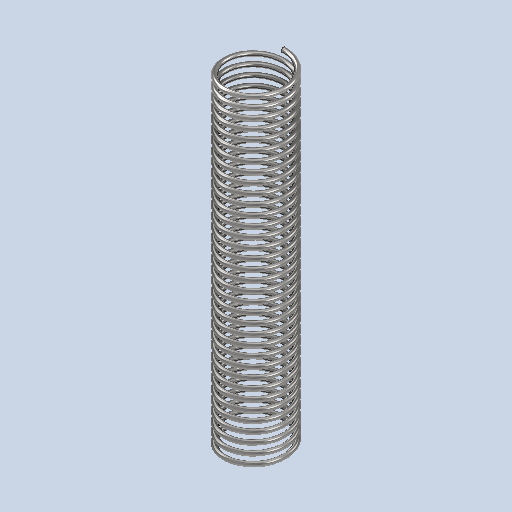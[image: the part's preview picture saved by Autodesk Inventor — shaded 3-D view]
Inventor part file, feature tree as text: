
AUTODESK INVENTOR PART (.ipt)
format: ipt  version: 2025 (Build 290162010, 162A)  size: 1,893,376 bytes
history: native  units: mm
features: sketch x97, plane x32, other x32, sweep x22, extrude x10, helix x4
ambient origin geometry x8: Origin, YZ Plane, XZ Plane, XY Plane, X Axis, Y Axis, Z Axis, Center Point
bodies: Solid1 (feature_tree)
feature tree (197):
  sketch  "3D Sketch2"
  plane  "ArbeitsebeneSweeping1"
  sweep  "Sweep1"
  other  "Erste Umdrehung mit Ösentyp 0(Rechts)"
  sketch  "Sketch8"  dims[d5=0.0mm d6=90.0deg d7=90.0deg d8=0.0mm d9=0.0mm d12=0.2mm]
  plane  "ArbeitsebeneExtrusion7"
  sketch  "Sketch10"  dims[d17=90.0deg d24=0.0mm d25=0.39411mm]
  plane  "ArbeitsebeneSweeping2"
  sweep  "Sweep2"
  other  "Zweite Umdrehung mit Ösentyp 0(Rechts)"
  sketch  "Sketch12"  dims[d26=10.0mm d27=347.619048mm]
  plane  "ArbeitsebeneExtrusion8"
  sketch  "Sketch110"  dims[d396=50.0mm]
  sketch  "3D Sketch20"
  plane  "ArbeitsebeneSweeping3"
  sweep  "Sweep3"
  sketch  "3D Sketch3"
  plane  "ArbeitsebeneSweeping6"
  sweep  "Sweep6"
  other  "Erste Umdrehung mit Ösentyp 0(Links)"
  sketch  "Sketch24"  dims[d171=0.0mm d172=90.0deg]
  plane  "ArbeitsebeneExtrusion5"
  sketch  "Sketch18"  dims[d86=90.0deg d87=20.0mm d90=20.0mm]
  plane  "ArbeitsebeneSweeping7"
  sweep  "Sweep7"
  other  "Zweite Umdrehung mit Ösentyp 0(Links)"
  sketch  "Sketch20"  dims[d149=90.0deg d152=20.0mm]
  plane  "ArbeitsebeneExtrusion6"
  sketch  "Sketch22"  dims[d169=300.0deg d170=1.075mm]
  plane  "ArbeitsebeneSweeping8"
  sweep  "Sweep8"
  other  "Erste Umdrehung mit Ösentyp 1(Links)"
  sketch  "Sketch27"  dims[d175=0.0mm d176=300.0deg]
  plane  "ArbeitsebeneExtrusion9"
  extrude  "Extrusion9"  Depth=10.0mm
  sketch  "Sketch29"  dims[d179=30.0mm d180=90.0deg]
  plane  "ArbeitsebeneSweeping9"
  sweep  "Sweep9"
  other  "Zweite Umdrehung mit Ösentyp 1(Links)"
  sketch  "Sketch32"  dims[d183=0.0mm d184=30.0mm d185=30.0mm d186=30.0mm]
  plane  "ArbeitsebeneExtrusion10"
  sketch  "Sketch34"  dims[d189=1.25mm d190=0.0mm]
  sketch  "3D Sketch22"
  plane  "ArbeitsebeneSweeping10"
  sweep  "Sweep10"
  other  "Erste Umdrehung mit Ösentyp 1(Rechts)"
  sketch  "Sketch42"  dims[d195=40.0mm d196=1.25mm]
  plane  "ArbeitsebeneExtrusion11"
  extrude  "Extrusion11"  Depth=20.0mm
  sketch  "Sketch44"  dims[d199=300.0deg d200=1.075mm]
  plane  "ArbeitsebeneSweeping11"
  sweep  "Sweep11"
  other  "Zweite Umdrehung mit Ösentyp 1(Rechts)"
  sketch  "Sketch112"  dims[d397=29.670597mm]
  plane  "ArbeitsebeneExtrusion12"
  sketch  "Sketch114"  dims[d401=50.0mm]
  sketch  "3D Sketch24"
  plane  "ArbeitsebeneSweeping12"
  sweep  "Sweep12"
  sketch  "Sketch46"  dims[d201=0.0mm d202=90.0deg]
  other  "Erstes Sweeping mit Ösentyp 2(Links)"
  sweep  "SweepingLinksÖse21"
  sketch  "Sketch48"  dims[d206=300.0deg d207=1.075mm]
  other  "Zweites Sweeping mit Ösentyp 2(Links)"
  sweep  "SweepingLinksÖse22"
  sketch  "Sketch50"  dims[d210=1.25mm d211=0.0mm d212=90.0deg d213=300.0deg d214=1.075mm]
  other  "Erstes Sweeping mit Ösentyp 2(Rechts)"
  sweep  "SweepingRechtsÖse21"
  sketch  "Sketch52"  dims[d220=50.0mm]
  other  "Zweites Sweeping mit Ösentyp 2(Rechts)"
  sweep  "SweepingRechtsÖse22"
  other  "Erste Umdrehung mit Ösentyp 3(Links)"
  extrude  "Extrusion1"  TaperAngle=90.0deg  [1 undecoded]
  sweep  "Sweep19"
  other  "Zweite Umdrehung mit Ösentyp 3(Links)"
  extrude  "Extrusion2"  Depth=30.0mm
  sketch  "Sketch60"  dims[d242=90.0deg]
  plane  "ArbeitsebeneSweeping20"
  sweep  "Sweep20"
  other  "Erste Umdrehung mit Ösentyp 3(Rechts)"
  extrude  "Extrusion3"  TaperAngle=0.0deg  [1 undecoded]
  sweep  "Sweep21"
  other  "Zweite Umdrehung mit Ösentyp 3(Rechts)"
  extrude  "Extrusion4"  TaperAngle=90.0deg  [1 undecoded]
  sketch  "Sketch68"  dims[d282=60.0mm]
  plane  "Work Plane46"
  sweep  "Sweep22"
  other  "Erste Umdrehung mit Ösentyp 4(Links)"
  sketch  "Sketch71"  dims[d301=10.0mm d302=15.0mm d303=0.0mm d304=90.0deg d305=90.0deg d306=0.0mm d307=0.0mm]
  plane  "ArbeitsebeneExtrusion13"
  extrude  "Extrusion13"  TaperAngle=90.0deg  [1 undecoded]
  sketch  "Sketch73"  dims[d310=0.7mm]
  plane  "ArbeitsebeneSweeping23"
  sweep  "Sweep23"
  other  "Zweite Umdrehung mit Ösentyp 4(Links)"
  sketch  "Sketch76"  dims[d320=1.125mm]
  plane  "ArbeitsebeneExtrusion14"
  sketch  "Sketch78"  dims[d322=10.0mm d323=15.0mm d324=0.0mm d325=90.0deg d326=90.0deg d327=0.0mm d328=0.0mm d329=70.0mm]
  sketch  "3D Sketch26"
  plane  "ArbeitsebeneSweeping24"
  sweep  "Sweep24"
  other  "Erste Umdrehung mit Ösentyp 4(Rechts)"
  sketch  "Sketch86"  dims[d332=10.0mm d333=15.0mm d334=0.0mm d335=90.0deg d336=90.0deg d337=0.0mm d338=0.0mm d339=70.0mm]
  plane  "Work PlaneExtrusion15"
  extrude  "Extrusion15"  Depth=1.25mm TaperAngle=0.0deg
  sketch  "Sketch88"  dims[d361=10.0mm]
  plane  "ArbeitsebeneSweeping25"
  sweep  "Sweep25"
  other  "Zweite Umdrehung mit Ösentyp 4(Rechts)"
  sketch  "Sketch116"  dims[d404=1.0mm]
  plane  "ArbeitsebeneExtrusion16"
  sketch  "Sketch118"  dims[d406=50.0mm d407=29.670597mm d408=0.0mm d411=60.0mm d423=60.0mm d433=1.0mm d434=0.0mm d435=1.075mm d436=0.7mm d437=10.0mm d438=15.0mm d439=0.0mm d440=90.0deg d441=90.0deg d442=0.0mm d443=0.0mm d444=60.0mm d447=60.0mm d457=1.0mm d458=0.0mm d459=60.0mm d469=90.0deg d478=90.0deg d479=1.075mm d480=0.7mm d481=25.4mm d482=15.0mm d483=0.0mm d484=90.0deg d485=90.0deg d486=0.0mm d487=0.0mm d491=10.0mm d498=10.0mm d501=0.0mm d502=1.0mm d503=0.0mm d504=210.0deg d505=0.0mm d506=0.0mm d507=1.0mm d508=0.0mm d509=29.670597mm d510=0.0mm d511=10.0mm d512=0.0mm d513=1.0mm d514=0.0mm d515=29.670597mm d516=0.0mm d517=0.0mm d518=1.0mm d519=0.0mm d520=1.075mm d521=0.7mm d522=10.0mm d523=15.0mm d524=0.0mm d525=90.0deg d526=90.0deg d527=0.0mm d528=0.0mm d529=60.0mm d530=50.0mm d531=0.0mm d532=1.0mm d533=0.0mm d534=20.0mm d535=210.0deg d536=0.0mm d537=0.0mm d538=1.0mm d539=0.0mm d540=29.670597mm d541=0.0mm d542=50.0mm d543=0.0mm d544=1.0mm d545=0.0mm d546=60.0mm d547=1.075mm d548=0.7mm d549=10.0mm d550=15.0mm d551=0.0mm d552=90.0deg d553=90.0deg d554=0.0mm d555=0.0mm d561=10.0mm d564=0.0mm d565=1.0mm d566=0.0mm d567=10.0mm d569=29.670597mm d570=0.0mm d571=90.0deg d578=0.0mm d579=0.2mm d580=1.0mm d581=0.0mm d584=10.0mm d585=10.0mm d588=29.670597mm d589=0.0mm d590=0.0mm d591=0.0mm d592=0.0mm d593=0.0mm d594=0.0mm d595=0.0mm d596=0.0mm d597=0.0mm d598=0.0mm d599=0.0mm d600=0.0mm d601=0.0mm d602=0.0mm d603=0.0mm d604=0.0mm d605=0.0mm d606=0.0mm d607=0.0mm d608=0.0mm d609=0.0mm d610=0.0mm d611=0.0mm]
  sketch  "3D Sketch28"
  plane  "ArbeitsebeneSweeping26"
  sweep  "Sweep26"
  other  "Erste Umdrehung mit Ösentyp 5(Links)"
  sketch  "Sketch91"  dims[d365=0.0mm]
  plane  "ArbeitsebeneExtrusion17"
  extrude  "Extrusion17"  TaperAngle=0.0deg  [1 undecoded]
  helix  "Coil1"  [1 undecoded]
  other  "Zweite Umdrehung mit Ösentyp 5(Links)"
  sketch  "Sketch95"  dims[d373=20.0mm]
  plane  "ArbeitsebeneExtrusion18"
  helix  "Coil2"  [1 undecoded]
  other  "Erste Umdrehung mit Ösentyp 5(Rechts)"
  sketch  "Sketch99"  dims[d377=210.0deg]
  plane  "ArbeitsebeneExtrusion19"
  helix  "Coil13"  [1 undecoded]
  other  "Zweite Umdrehung mit Ösentyp 5(Rechts)"
  sketch  "Sketch103"  dims[d385=0.0mm]
  plane  "ArbeitsebeneExtrusion20"
  extrude  "Extrusion20"  Depth=40.0mm
  sketch  "Sketch105"  dims[d387=210.0deg]
  helix  "Coil4"  [1 undecoded]
  other  "Erste Spirale mit Ösentyp 6(Links)"
  other  "Zweite Spirale mit Ösentyp 6(Links)"
  other  "Erste Spirale mit Ösentyp 6(Rechts)"
  other  "Zweite Spirale mit Ösentyp 6(Rechts)"
  other  "Srf1"
  sketch  "Sketch4"  dims[d0=0.05mm d1=1.25mm]
  sketch  "Sketch7"  dims[d2=0.39411mm d3=10.0mm d4=347.619048mm]
  other  "Srf2"
  sketch  "Sketch16"  dims[d38=90.0deg d54=10.0mm d55=10.0mm]
  sketch  "Sketch26"  dims[d173=300.0deg d174=1.075mm]
  sketch  "Sketch31"  dims[d181=300.0deg d182=1.125mm]
  sketch  "Sketch36"  dims[d191=300.0deg d192=1.075mm]
  sketch  "Sketch41"  dims[d193=0.0mm d194=90.0deg]
  sketch  "Sketch47"  dims[d203=40.0mm d204=1.25mm d205=0.0mm]
  sketch  "Sketch49"  dims[d208=0.0mm d209=90.0deg]
  sketch  "Sketch51"  dims[d215=0.0mm d216=40.0mm d217=90.0deg]
  sketch  "Sketch53"  dims[d223=90.0deg]
  sketch  "Sketch54"  dims[d226=50.0mm]
  sketch  "Sketch55"  dims[d229=90.0deg]
  sketch  "Sketch56"  dims[d232=50.0mm]
  sketch  "Sketch58"  dims[d235=90.0deg]
  sketch  "Sketch59"  dims[d238=50.0mm]
  sketch  "Sketch61"  dims[d243=60.0mm]
  sketch  "Sketch62"  dims[d255=90.0deg]
  sketch  "Sketch63"  dims[d256=60.0mm]
  sketch  "Sketch64"  dims[d268=90.0deg]
  sketch  "Sketch66"  dims[d269=60.0mm]
  sketch  "Sketch67"  dims[d281=90.0deg]
  sketch  "Sketch69"  dims[d299=1.125mm]
  sketch  "Sketch70"  dims[d300=0.7mm]
  sketch  "Sketch75"  dims[d311=10.0mm d312=15.0mm d313=0.0mm d314=90.0deg d315=90.0deg d316=0.0mm d317=0.0mm d318=70.0mm d319=70.0mm]
  sketch  "Sketch80"  dims[d330=1.125mm]
  sketch  "Sketch85"  dims[d331=0.7mm]
  sketch  "Sketch90"  dims[d364=1.0mm]
  sketch  "Sketch94"  dims[d368=0.0mm]
  sketch  "Sketch98"  dims[d376=20.0mm]
  sketch  "Sketch102"  dims[d384=1.0mm]
  sketch  "Sketch106"  dims[d388=0.0mm]
  sketch  "Sketch107"  dims[d391=50.0mm]
  sketch  "Sketch108"  dims[d394=1.0mm]
  sketch  "Sketch109"  dims[d395=0.0mm]
  sketch  "Sketch13"  dims[d28=0.0mm d29=90.0deg d30=90.0deg d31=0.0mm d32=0.0mm d33=0.2mm]
  sketch  "Sketch33"  dims[d187=90.0deg d188=40.0mm]
  sketch  "Sketch113"  dims[d398=0.0mm]
  sketch  "Sketch77"  dims[d321=0.7mm]
  sketch  "Sketch117"  dims[d405=0.0mm]
  sketch  "Sketch96"  dims[d374=1.0mm]
  sketch  "Sketch97"  dims[d375=0.0mm]
  sketch  "Sketch104"  dims[d386=20.0mm]
  sketch  "Sketch43"  dims[d197=0.0mm d198=90.0deg]
  sketch  "Sketch9"  dims[d13=0.0mm d14=90.0deg]
  sketch  "Sketch87"  dims[d350=10.0mm d352=10.0mm d353=10.0mm d356=10.0mm]
  sketch  "Sketch100"  dims[d378=0.0mm]
  sketch  "Sketch101"  dims[d381=20.0mm]
  sketch  "Sketch28"  dims[d177=1.125mm d178=0.0mm]
  sketch  "Sketch72"  dims[d308=1.125mm]
  sketch  "Sketch92"  dims[d366=10.0mm]
  sketch  "Sketch93"  dims[d367=29.670597mm]
  sketch  "Sketch21"  dims[d155=90.0deg d156=20.0mm]
  sketch  "Sketch15"  dims[d34=0.0mm d36=0.0mm]
  sketch  "Sketch17"  dims[d72=0.0mm d73=0.0mm d79=90.0deg]
  other  "Basisschraube(Rechts)"
  other  "Basisschraube(Links)"
note: 9 required parameter values undecoded (feature->parameter linkage not recoverable at this tier; creation-order binding heuristic only, values carry confidence <= 0.55)
